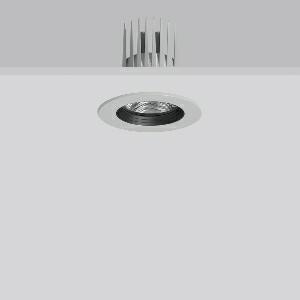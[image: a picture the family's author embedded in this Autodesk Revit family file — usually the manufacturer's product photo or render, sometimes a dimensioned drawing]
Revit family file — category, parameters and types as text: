
# Revit family: heledon_mini_e_901741_004_7f34
name_source: partatom
category: Lighting Fixtures
units: mm (PartAtom-declared; Revit-internal decimal feet)

## family parameters
Cut with Voids When Loaded = No
Host = Face
Light Source = No
Part Type = Normal
Room Calculation Point = No
Round Connector Dimension = Use Diameter
Shared = No

## types (1)
- HELEDON mini E (1 x LED Modul 930, 2450 lm, 3000)
    Apparent Load = 20 VA
    Approval mark = CE
    CIE Flux Codes = 99 100 100 100 100
    Color Rendering = 90
    Color Temperature = 3000
    Default Elevation = 1800 mm
    Description = Series: HELEDON mini
Round recessed downlight. Housing: die-cast aluminium, powder-coated. Black plastic ring and recessed LED to prevent glare from the side. Optical assembly with reflector made of MIRO-Silver with 98% total light reflection for outstanding efficiency - can be changed without tools. Best colour rendering index Ra>90. Suitable for Recessed ceiling mounting. Installation without tools thanks to spring fastening system. Including separate LED converter with connecting cable 600 mm.High quality converter without flickering and stroboscopic effect. Through-wiring box (5 pole) available as accessory. The following accessories can be mounted without use of tools: interchangeable lenses, decorative glasses, honeycomb louvre, clear and frosted diffusers, white interchangeable plastic ring. 
Colour: silver
Diameter: 124 mm
Height: 3 mm
Cut-out diameter: 114 mm
Recess height: 170 mm
Luminaire: recess height: 120 mm
Lamp: LED
Socket: without socket
Colour temperature: 3000K
Colour rendering index (CRI): 92
System power: 20 W
Rated luminous flux: 2450 lm
Luminous efficiency: 123 lm/W
Control gear: Regulated power supply
Protection class: II
Type of protection: IP 20
    Height = 0 mm  [stored 0 ft]
    Lamp = 1 x LED Modul 930
    Lamp Light Flux = 2450 lm
    Lamp count = 1
    Length = 124 mm  [stored 0.406824 ft]
    Lifetime = 50000 h
    Luminous efficacy = 123 lm/W
    Manufacturer = RZB
    ModVariant = No
    Model = 901741.004
    Mounting Place = Ceiling
    Mounting Type = Recessed
    Number of Poles = 1
    OnlyDefault = Yes
    Power Factor = 1
    Product Name = HELEDON mini E
    Product group = Recessed downlights
    ProductGroupID = 402
    Protection Class = Protection class II
    Protection Degree = IP 20
    RLX_Detail_Level = 1
    RLX_Emergency_Light_Flux = 0 lm
    RLX_Emergency_Type = 0
    RLX_Emergency_Type_DB = No
    RlxData = <blob elided: 126765 chars, md5=17245fd0>
    Socket = socket
    Standby Power = 0 W
    System Light Flux = 2450 lm
    System Power = 20 W
    Type Comments = Product without accessories
    Type Image = 901657.004.jpg
    URL = http://relux.com
    VarID = ---
    Voltage = 230 V
    Voltage Range = 220-240 V
    Weight = 0.00 kg
    Width = 0 mm  [stored 0 ft]

note: [stored X ft] marks values corroborated as IEEE doubles in the binary element streams (Revit-internal decimal feet)

## geometry (parser evidence)
native form markers: Blend x4, Sweep x11
no freeform markers — native parametric forms only
